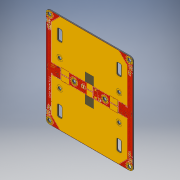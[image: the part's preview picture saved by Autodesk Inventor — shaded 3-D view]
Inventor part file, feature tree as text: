
AUTODESK INVENTOR PART (.ipt)
format: ipt  version: 2018 (Build 220112000, 112)  size: 943,104 bytes
history: native  units: mm
features: sketch x6, other x4, hole x3, extrude x1
ambient origin geometry x8: Origin, YZ Plane, XZ Plane, XY Plane, X Axis, Y Axis, Z Axis, Center Point
bodies: Solid1 (feature_tree)
feature tree (14):
  extrude  "Extrusion1"  Depth=90.0mm
  other  "Decal3"
  other  "Decal4"
  hole  "Hole5"  [1 undecoded]
  hole  "Hole6"  [1 undecoded]
  hole  "Hole7"  [1 undecoded]
  sketch  "Sketch1"  dims[d0=79.0mm d1=90.0mm]
  sketch  "Sketch8"  dims[d2=3.0mm d3=3.3mm]
  sketch  "Sketch9"  dims[d4=28.0mm d5=1.0mm d6=0.0mm]
  sketch  "Sketch10"  dims[d92=29.0mm d93=35.0mm]
  sketch  "Sketch11"  dims[d94=25.0mm]
  sketch  "Sketch12"  dims[d95=25.0mm d96=1.0mm d103=3.0mm d104=6.0mm d105=4.0mm d106=2.0mm d107=90.0deg d108=8.0mm d109=20.594885mm d110=0.45mm d111=6.0mm d112=4.0mm d113=2.0mm d114=90.0deg d115=8.0mm d116=20.594885mm d117=0.3mm d118=6.0mm d119=4.0mm d120=2.0mm d121=90.0deg d122=8.0mm d123=20.594885mm]
  other  "Image16"
  other  "Image17"
note: 3 required parameter values undecoded (feature->parameter linkage not recoverable at this tier; creation-order binding heuristic only, values carry confidence <= 0.55)
